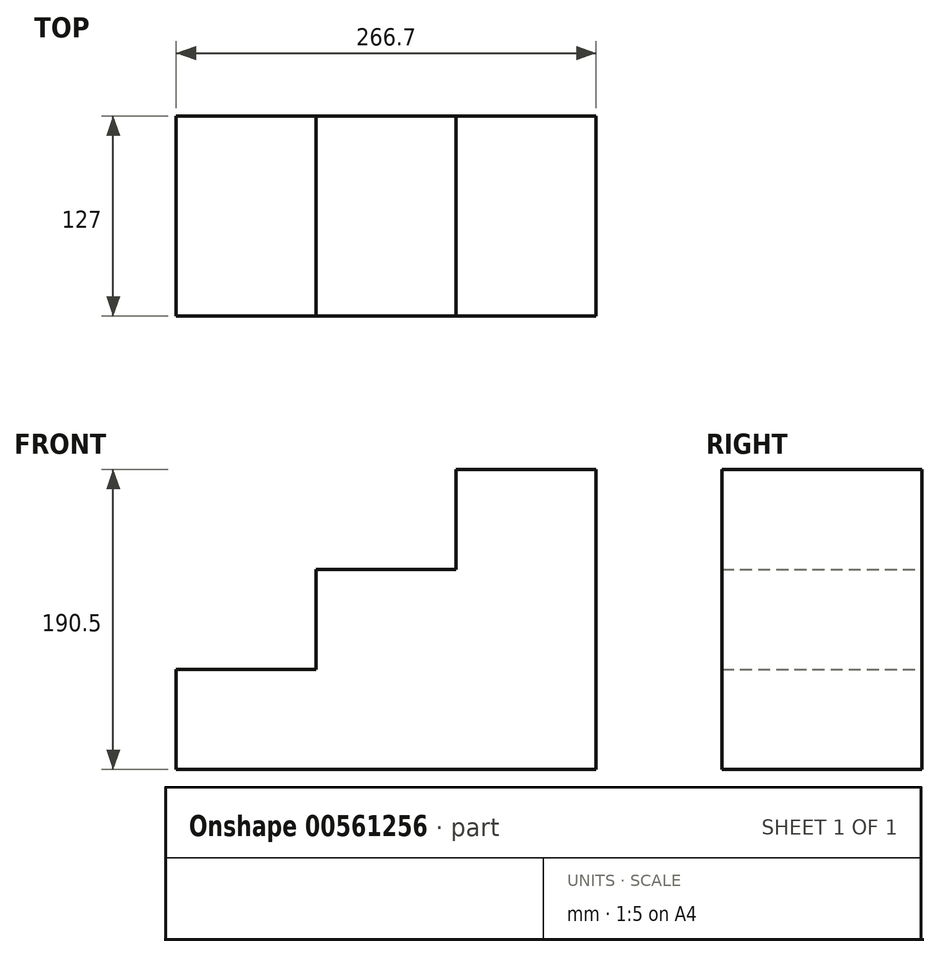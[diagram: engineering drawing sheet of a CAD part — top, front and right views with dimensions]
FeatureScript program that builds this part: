
annotation { "Feature Type Name" : "Feature", "Feature Type Description" : "" }
export const myFeature = defineFeature(function(context is Context, id is Id, definition is map)
    precondition{}
    {
        {
            var Q0;
            Q0=qCreatedBy(makeId("Front.planeOp"),FACE);
            var sketch = newSketch(context, id + "F0", { "sketchPlane" : qUnion([Q0])});
            skLineSegment(sketch, "E0", {"start": v(-76.77, -75.53) * mm, "end": v(189.93, -75.53) * mm});
            skLineSegment(sketch, "E1", {"start": v(189.93, -75.53) * mm, "end": v(189.93, 114.97) * mm});
            skLineSegment(sketch, "E2", {"start": v(189.93, 114.97) * mm, "end": v(101.03, 114.97) * mm});
            skLineSegment(sketch, "E3", {"start": v(101.03, 114.97) * mm, "end": v(101.03, 51.47) * mm});
            skLineSegment(sketch, "E4", {"start": v(101.03, 51.47) * mm, "end": v(12.13, 51.47) * mm});
            skLineSegment(sketch, "E5", {"start": v(12.13, 51.47) * mm, "end": v(12.13, -12.03) * mm});
            skLineSegment(sketch, "E6", {"start": v(12.13, -12.03) * mm, "end": v(-76.77, -12.03) * mm});
            skLineSegment(sketch, "E7", {"start": v(-76.77, -12.03) * mm, "end": v(-76.77, -75.53) * mm});
            skSolve(sketch);
        }
        {
            var Q0;
            Q0=makeQuery(id+"F0.imprint","IMPRINT",FACE,{"disambiguationData":[TD([[makeQuery(id+"F0.imprint","IMPRINT",EDGE,{"derivedFrom":sQuery(id+"F0.wireOp",EDGE,"E0")}),1.0]])]});
            extrude(context, id + "F1", {"entities" : qUnion([Q0]), "depth" : 127 * mm, "offsetDistance" : 25.4 * mm});
        }
    });
